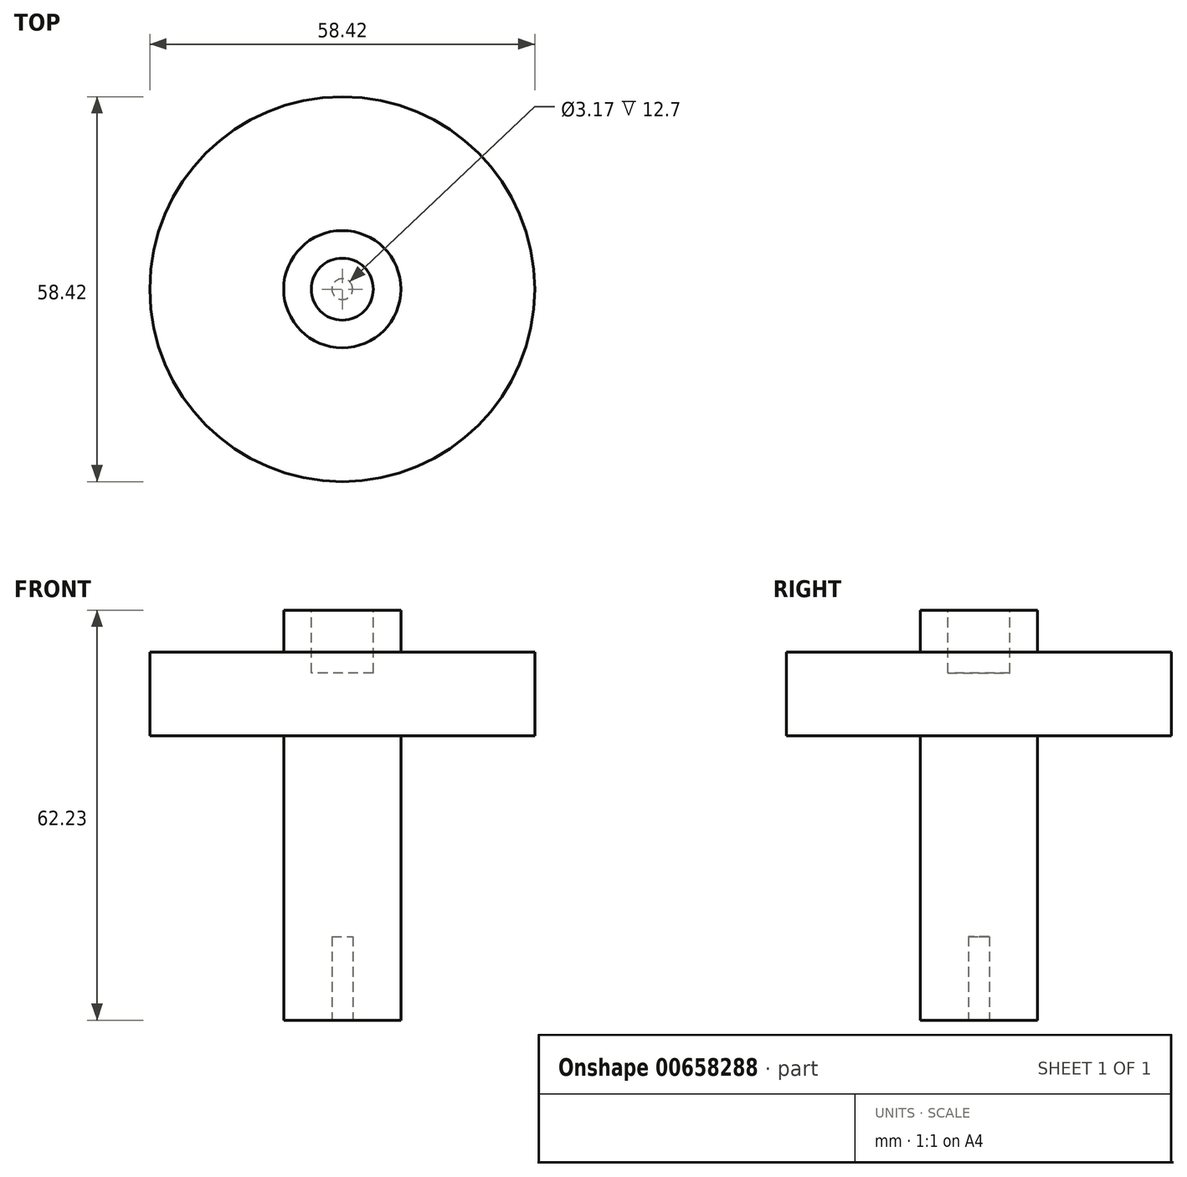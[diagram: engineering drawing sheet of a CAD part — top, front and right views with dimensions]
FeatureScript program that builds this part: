
annotation { "Feature Type Name" : "Feature", "Feature Type Description" : "" }
export const myFeature = defineFeature(function(context is Context, id is Id, definition is map)
    precondition{}
    {
        {
            var Q0;
            Q0=qCreatedBy(makeId("Front.planeOp"),FACE);
            var sketch = newSketch(context, id + "F0", { "sketchPlane" : qUnion([Q0])});
            skLineSegment(sketch, "E0", {"start": v(0, 0) * mm, "end": v(8.9, 0) * mm});
            skLineSegment(sketch, "E1", {"start": v(8.9, 0) * mm, "end": v(8.9, 43.18) * mm});
            skLineSegment(sketch, "E2", {"start": v(8.9, 43.18) * mm, "end": v(29.21, 43.18) * mm});
            skLineSegment(sketch, "E3", {"start": v(29.21, 43.18) * mm, "end": v(29.21, 55.88) * mm});
            skLineSegment(sketch, "E4", {"start": v(29.21, 55.88) * mm, "end": v(8.9, 55.88) * mm});
            skLineSegment(sketch, "E5", {"start": v(8.9, 55.88) * mm, "end": v(8.9, 62.23) * mm});
            skLineSegment(sketch, "E6", {"start": v(8.9, 62.23) * mm, "end": v(0, 62.23) * mm});
            skLineSegment(sketch, "E7", {"start": v(0, 62.23) * mm, "end": v(0, 0) * mm});
            skSolve(sketch);
        }
        {
            var Q0;
            Q0 = qSketchRegion(id + "F0", true);
            var Q1;
            Q1=sQuery(id+"F0.wireOp",EDGE,"E7");
            revolve(context, id + "F1", {"entities" : qUnion([Q0]), "axis" : qUnion([Q1]), "revolveType" : RevolveType.FULL});
        }
        {
            var Q0;
            Q0=makeQuery(id+"F1.opRevolve","SWEPT_FACE",FACE,{"disambiguationData":[OSD([sQuery(id+"F0.wireOp",EDGE,"E6")])]});
            var sketch = newSketch(context, id + "F2", { "sketchPlane" : qUnion([Q0])});
            skCircle(sketch, "E8", {"center": v(0, 0) * mm, "radius": 4.7 * mm});
            skSolve(sketch);
        }
        {
            var Q0;
            Q0 = qSketchRegion(id + "F2", true);
            extrude(context, id + "F3", {"entities" : qUnion([Q0]), "operationType" : NewBodyOperationType.REMOVE, "oppositeDirection" : true, "depth" : 9.52 * mm, "offsetDistance" : 25.4 * mm});
        }
        {
            var Q0;
            Q0=makeQuery(id+"F1.opRevolve","SWEPT_FACE",FACE,{"disambiguationData":[OSD([sQuery(id+"F0.wireOp",EDGE,"E0")])]});
            var sketch = newSketch(context, id + "F4", { "sketchPlane" : qUnion([Q0])});
            skCircle(sketch, "E9", {"center": v(0, 0) * mm, "radius": 1.59 * mm});
            skSolve(sketch);
        }
        {
            var Q0;
            Q0 = qSketchRegion(id + "F4", true);
            extrude(context, id + "F5", {"entities" : qUnion([Q0]), "operationType" : NewBodyOperationType.REMOVE, "oppositeDirection" : true, "depth" : 12.7 * mm, "offsetDistance" : 25.4 * mm});
        }
    });
